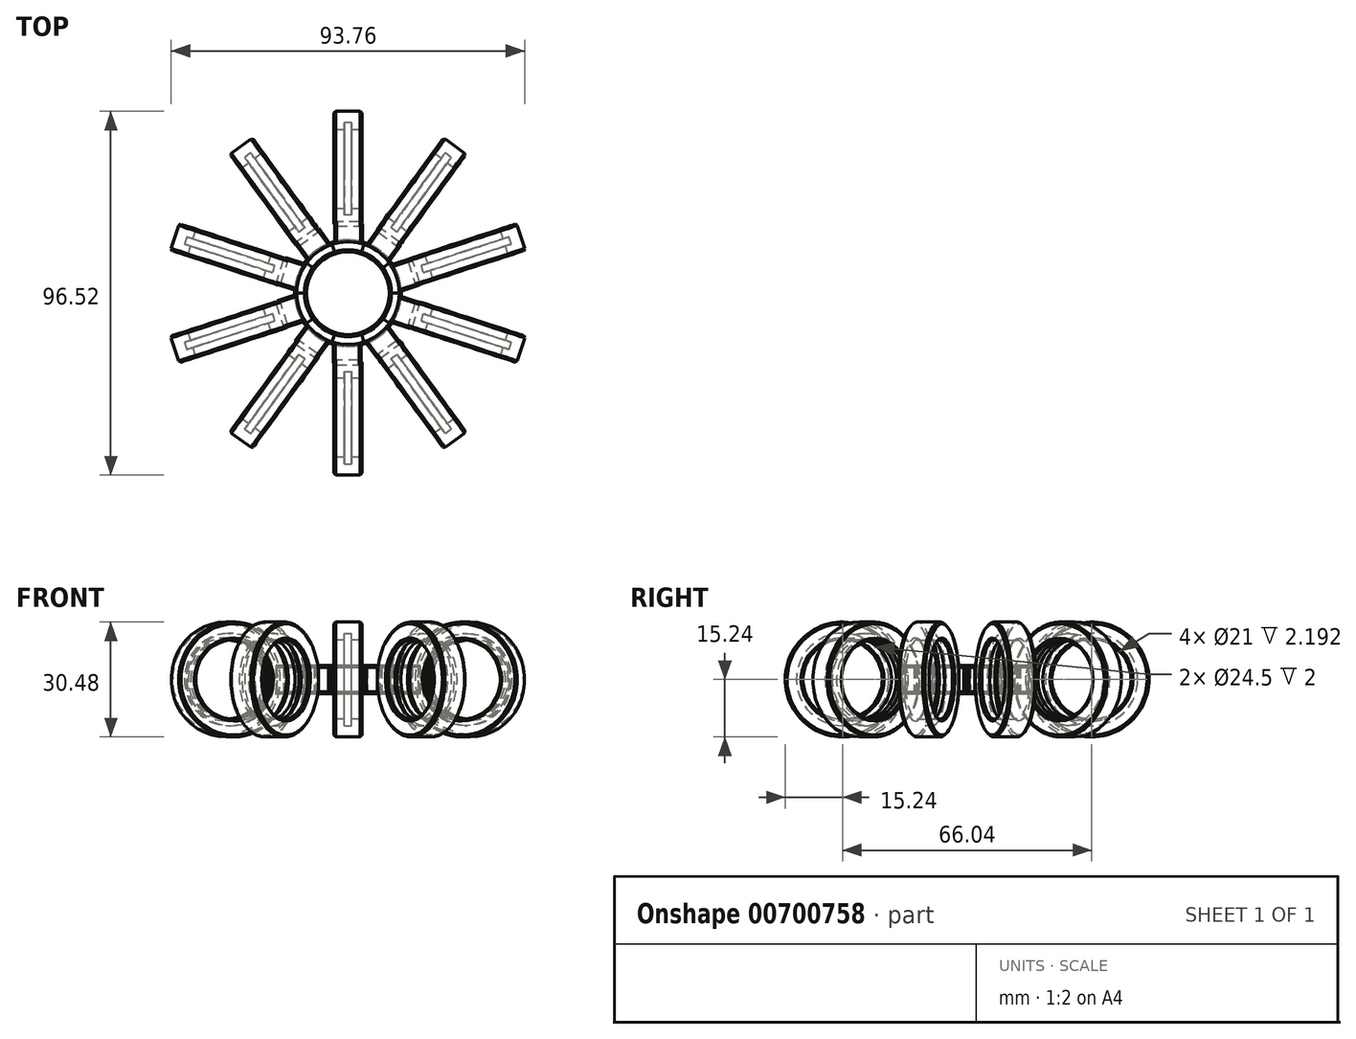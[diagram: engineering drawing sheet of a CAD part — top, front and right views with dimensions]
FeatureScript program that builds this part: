
annotation { "Feature Type Name" : "Feature", "Feature Type Description" : "" }
export const myFeature = defineFeature(function(context is Context, id is Id, definition is map)
    precondition{}
    {
        {
            var Q0;
            Q0=qCreatedBy(makeId("Top.planeOp"),FACE);
            var sketch = newSketch(context, id + "F0", { "sketchPlane" : qUnion([Q0])});
            skArc(sketch, "E0", {"start": v(-11, 0) * mm, "mid": v(0, -11) * mm, "end": v(11, 0) * mm});
            skArc(sketch, "E1", {"start": v(3.55, -13.68) * mm, "mid": v(11.17, -8.65) * mm, "end": v(14.13, 0) * mm});
            skLineSegment(sketch, "E2.top", {"start": v(-3.85, -19) * mm, "end": v(3.55, -19) * mm});
            skLineSegment(sketch, "E2.left", {"start": v(-3.85, -13.6) * mm, "end": v(-3.85, -19) * mm});
            skLineSegment(sketch, "E2.right", {"start": v(3.55, -13.6) * mm, "end": v(3.55, -19) * mm});
            skLineSegment(sketch, "E3", {"start": v(14.13, 0) * mm, "end": v(11, 0) * mm});
            skArc(sketch, "E4.trimOffspring", {"start": v(-14.13, 0) * mm, "mid": v(-11.27, -8.52) * mm, "end": v(-3.85, -13.6) * mm});
            skLineSegment(sketch, "E5.trimOffspring", {"start": v(-11, 0) * mm, "end": v(-14.13, 0) * mm});
            skSolve(sketch);
        }
        {
            var Q0;
            Q0=makeQuery(id+"F0.imprint","IMPRINT",FACE,{"disambiguationData":[TD([[makeQuery(id+"F0.imprint","IMPRINT",EDGE,{"derivedFrom":sQuery(id+"F0.wireOp",EDGE,"E0")}),-1.0]])]});
            var Q1;
            {var subQ4=sQuery(id+"F0.wireOp",EDGE,"E2.top");Q1=makeQuery(id+"F0.imprint","IMPRINT",FACE,{"disambiguationData":[TD([[makeQuery(id+"F0.imprint","IMPRINT",EDGE,{"derivedFrom":subQ4}),1.0]])]});}
            extrude(context, id + "F1", {"entities" : qUnion([Q0, Q1]), "endBound" : BoundingType.SYMMETRIC, "depth" : 7.5 * mm, "offsetDistance" : 25.4 * mm});
        }
        {
            var Q0;
            Q0=qCreatedBy(makeId("Right.planeOp"),FACE);
            var sketch = newSketch(context, id + "F2", { "sketchPlane" : qUnion([Q0])});
            skCircle(sketch, "E6", {"center": v(-33.02, 0) * mm, "radius": 10.5 * mm});
            skCircle(sketch, "E7", {"center": v(-33.02, 0) * mm, "radius": 15.24 * mm});
            skSolve(sketch);
        }
        {
            var Q0;
            Q0=makeQuery(id+"F2.imprint","IMPRINT",FACE,{"disambiguationData":[TD([[makeQuery(id+"F2.imprint","IMPRINT",EDGE,{"derivedFrom":sQuery(id+"F2.wireOp",EDGE,"E6")}),-1.0]])]});
            extrude(context, id + "F3", {"entities" : qUnion([Q0]), "endBound" : BoundingType.SYMMETRIC, "depth" : 7.4 * mm, "offsetDistance" : 25.4 * mm});
        }
        {
            var Q0;
            Q0=qCreatedBy(makeId("Right.planeOp"),FACE);
            var sketch = newSketch(context, id + "F4", { "sketchPlane" : qUnion([Q0])});
            skCircle(sketch, "E8", {"center": v(-33.02, 0) * mm, "radius": 12.25 * mm});
            skSolve(sketch);
        }
        {
            var Q0;
            Q0 = qSketchRegion(id + "F4", true);
            extrude(context, id + "F5", {"entities" : qUnion([Q0]), "operationType" : NewBodyOperationType.REMOVE, "endBound" : BoundingType.SYMMETRIC, "oppositeDirection" : true, "depth" : 2 * mm, "offsetDistance" : 25.4 * mm});
        }
        {
            var Q0;
            Q0=makeQuery(id+"F3.opExtrude","CAP_FACE",FACE,{"disambiguationData":[OSD([sQuery(id+"F2.wireOp",EDGE,"E6"),sQuery(id+"F2.wireOp",EDGE,"E7")])],"isStart":true});
            var Q1;
            Q1=makeQuery(id+"F3.opExtrude","CAP_FACE",FACE,{"disambiguationData":[OSD([sQuery(id+"F2.wireOp",EDGE,"E6"),sQuery(id+"F2.wireOp",EDGE,"E7")])],"isStart":false});
            var Q2;
            Q2=makeQuery(id+"F1.opExtrude","CAP_EDGE",EDGE,{"disambiguationData":[OSD([sQuery(id+"F0.wireOp",EDGE,"E1")])],"isStart":true});
            var Q3;
            Q3=makeQuery(id+"F1.opExtrude","CAP_EDGE",EDGE,{"disambiguationData":[OSD([sQuery(id+"F0.wireOp",EDGE,"E0")])],"isStart":true});
            var Q4;
            Q4=makeQuery(id+"F1.opExtrude","CAP_EDGE",EDGE,{"disambiguationData":[OSD([sQuery(id+"F0.wireOp",EDGE,"E4.trimOffspring")])],"isStart":true});
            var Q5;
            Q5=makeQuery(id+"F1.opExtrude","CAP_EDGE",EDGE,{"disambiguationData":[OSD([sQuery(id+"F0.wireOp",EDGE,"E2.right")])],"isStart":true});
            var Q6;
            Q6=makeQuery(id+"F1.opExtrude","CAP_EDGE",EDGE,{"disambiguationData":[OSD([sQuery(id+"F0.wireOp",EDGE,"E2.left")])],"isStart":true});
            var Q7;
            Q7=makeQuery(id+"F1.opExtrude","CAP_EDGE",EDGE,{"disambiguationData":[OSD([sQuery(id+"F0.wireOp",EDGE,"E2.left")])],"isStart":false});
            var Q8;
            Q8=makeQuery(id+"F1.opExtrude","CAP_EDGE",EDGE,{"disambiguationData":[OSD([sQuery(id+"F0.wireOp",EDGE,"E4.trimOffspring")])],"isStart":false});
            var Q9;
            Q9=makeQuery(id+"F1.opExtrude","CAP_EDGE",EDGE,{"disambiguationData":[OSD([sQuery(id+"F0.wireOp",EDGE,"E2.right")])],"isStart":false});
            var Q10;
            Q10=makeQuery(id+"F1.opExtrude","CAP_EDGE",EDGE,{"disambiguationData":[OSD([sQuery(id+"F0.wireOp",EDGE,"E1")])],"isStart":false});
            var Q11;
            Q11=makeQuery(id+"F1.opExtrude","CAP_EDGE",EDGE,{"disambiguationData":[OSD([sQuery(id+"F0.wireOp",EDGE,"E0")])],"isStart":false});
            chamfer(context, id + "F6", {"entities" : qUnion([Q0, Q1, Q2, Q3, Q4, Q5, Q6, Q7, Q8, Q9, Q10, Q11]), "width" : 0.5 * mm, "tangentPropagation" : true});
        }
        {
            var Q0;
            Q0=makeQuery(id+"F8.opPattern","COPY",EDGE,{"derivedFrom":makeQuery(id+"F1.opExtrude","SWEPT_EDGE",EDGE,{"disambiguationData":[OSD([sQuery(id+"F0.wireOp",EDGE,"E2.top"),sQuery(id+"F0.wireOp",EDGE,"E2.left")])]}),"instanceName":"1"});
            var Q1;
            Q1=makeQuery(id+"F1.opExtrude","SWEPT_EDGE",EDGE,{"disambiguationData":[OSD([sQuery(id+"F0.wireOp",EDGE,"E2.top"),sQuery(id+"F0.wireOp",EDGE,"E2.left")])]});
            chamfer(context, id + "F7", {"entities" : qUnion([Q0, Q1]), "width" : 0.5 * mm, "tangentPropagation" : true});
        }
        {
            var Q0;
            Q0=makeQuery(id+"F1.opExtrude","SWEPT_BODY",BODY,{"disambiguationData":[OSD([sQuery(id+"F0.wireOp",EDGE,"E0"),sQuery(id+"F0.wireOp",EDGE,"E1"),sQuery(id+"F0.wireOp",EDGE,"E2.top"),sQuery(id+"F0.wireOp",EDGE,"E2.left"),sQuery(id+"F0.wireOp",EDGE,"E2.right"),sQuery(id+"F0.wireOp",EDGE,"E3"),sQuery(id+"F0.wireOp",EDGE,"E4.trimOffspring"),sQuery(id+"F0.wireOp",EDGE,"E5.trimOffspring")])]});
            var Q1;
            Q1=makeQuery(id+"F3.opExtrude","SWEPT_BODY",BODY,{"disambiguationData":[OSD([sQuery(id+"F2.wireOp",EDGE,"E6"),sQuery(id+"F2.wireOp",EDGE,"E7")])]});
            var Q2;
            Q2=makeQuery(id+"F1.opExtrude","SWEPT_FACE",FACE,{"disambiguationData":[OSD([sQuery(id+"F0.wireOp",EDGE,"E0")])]});
            circularPattern(context, id + "F8", {"entities" : qUnion([Q0, Q1]), "axis" : qUnion([Q2]), "angle" : 360 * degree, "instanceCount" : 10, "equalSpace" : true});
        }
    });
